# Revit family: Panneaux équipés cuivre
name_source: partatom
category: Equipement spécialisé
units: mm (PartAtom-declared; Revit-internal decimal feet)

## family parameters
Basée sur le plan de construction = Non
Cote de connecteur circulaire = Utiliser le diamètre
Couper avec des vides une fois chargée = Non
Partagée = Oui
Point de calcul de pièce = Non
Toujours verticalement = Oui
Type d'élément = Normal

## types (8) — shared parameters
Classe d'application = EC001128
Couleur = IDS_NOIR
Dimension modulaire = 19 pouces
Fonction = Panneaux de brassage droits équipés
Indice de protection IK = IK03
Lien e-catalogue = https://www.legrand.fr
Maintien du câble = A chicane
Nature du câble pour connexion = Souple ou rigide
Nombre d'unités en hauteur = 1
Nombre de connecteurs = 24
RAL = 9017
Température de fonctionnement = -25°C à 70°C
Température de stockage = -40°C à 70°C
Type de connecteur = RJ45
Type de connexion = Contact pour connexion autodénudante
zero-valued in all types: Elévation par défaut

## per-type parameters (varying)
| type | Blindé | Catégorie | EAN | Hauteur | Largeur (mm) | Profondeur | Référence Legrand |
| Panneau équipé 24 RJ45 Cat 5e UTP 1U | Non | 5E | 3414970870308 | 43.85 mm  [stored 0.143865 ft] | 482.5 mm | 321.7 mm | 033750 |
| Panneau équipé 24 RJ45 Cat 5e FTP 1U | Oui | 5E | 3414970870322 | 43.85 mm  [stored 0.143865 ft] | 482.5 mm | 321.7 mm | 033751 |
| Panneau équipé 24 RJ45 Cat 6 UTP 1U | Non | 6 | 3414970870537 | 43.85 mm  [stored 0.143865 ft] | 482.5 mm | 321.7 mm | 033760 |
| Panneau équipé 24 RJ45 Cat 6 FTP 1U | Oui | 6 | 3414970870551 | 43.85 mm  [stored 0.143865 ft] | 482.5 mm | 321.7 mm | 033761 |
| Panneau équipé 24 RJ45 Cat 6 STP 1U | Oui | 6 | 3414970870575 | 43.85 mm  [stored 0.143865 ft] | 482.5 mm | 321.7 mm | 033762 |
| Panneau équipé 24 RJ45 Cat 6A UTP 1U | Non | 6A | 3414970870681 | 43.85 mm  [stored 0.143865 ft] | 482.5 mm | 321.7 mm | 033770 |
| Panneau équipé 24 RJ45 Cat 6A STP 1U | Oui | 6A | 3414970870704 | 43.85 mm  [stored 0.143865 ft] | 482.5 mm | 321.7 mm | 033772 |
| Panneau équipé 24 RJ45 Cat 8 STP 1U | Oui | 8 | 3414970982063 | 44.45 mm | 482.6 mm | 120 mm | 033782 |

note: column(s) folded — value = type name in every type: Libellé BIM

note: [stored X ft] marks values corroborated as IEEE doubles in the binary element streams (Revit-internal decimal feet)
